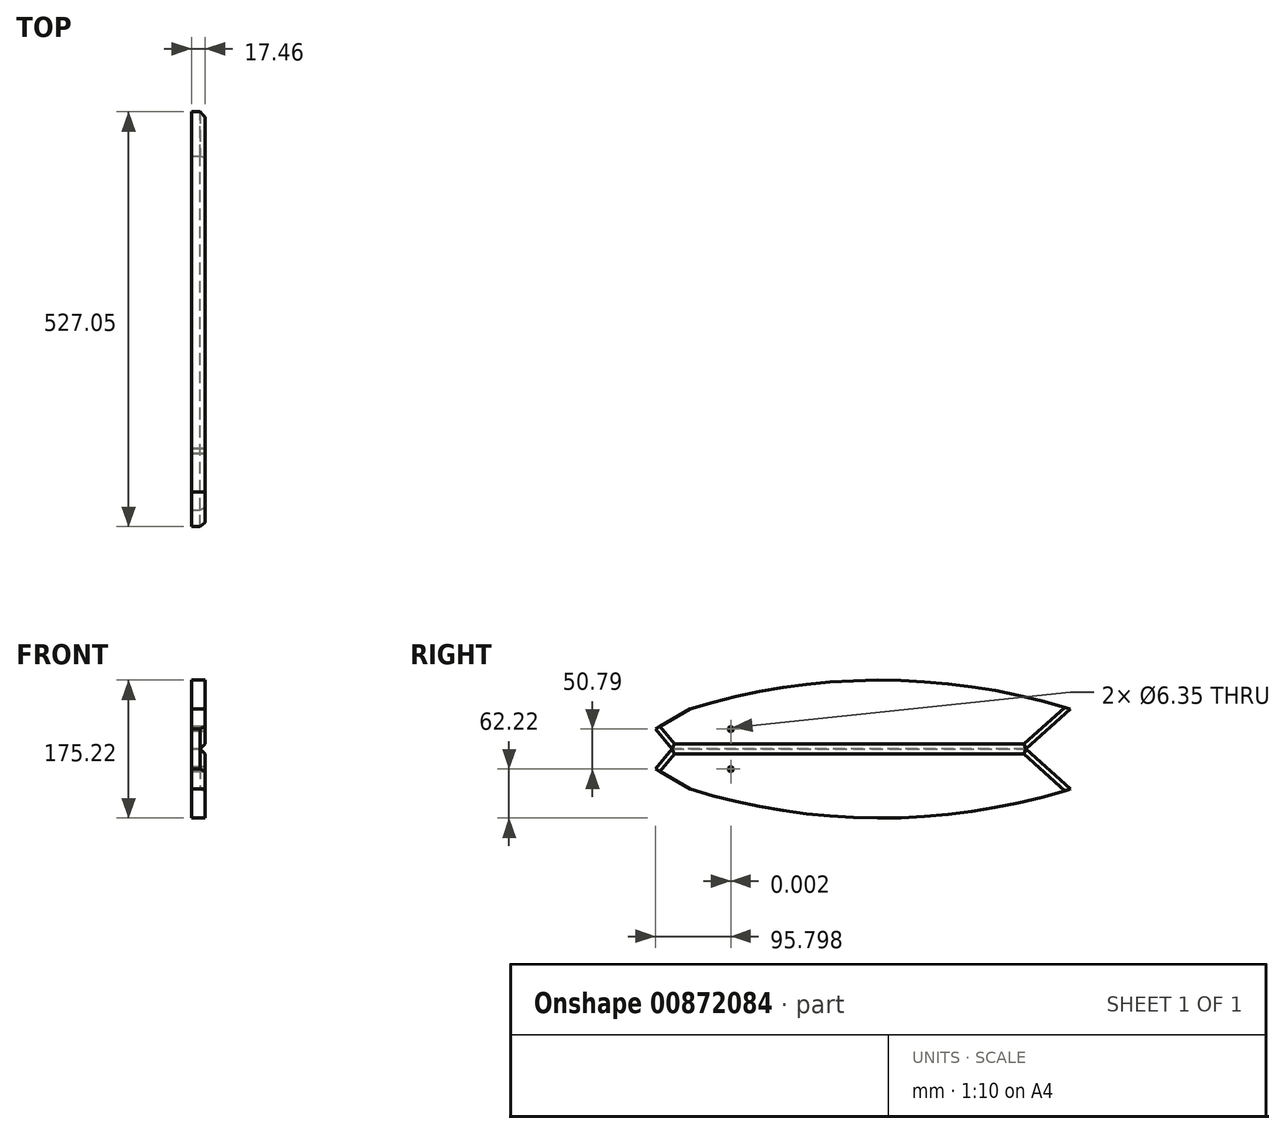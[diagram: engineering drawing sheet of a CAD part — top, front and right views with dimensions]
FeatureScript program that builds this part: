
annotation { "Feature Type Name" : "Feature", "Feature Type Description" : "" }
export const myFeature = defineFeature(function(context is Context, id is Id, definition is map)
    precondition{}
    {
        {
            var Q0;
            Q0=qCreatedBy(makeId("Right.planeOp"),FACE);
            var sketch = newSketch(context, id + "F0", { "sketchPlane" : qUnion([Q0])});
            skLineSegment(sketch, "E0.bottom", {"start": v(0, 0) * mm, "end": v(527.05, 0) * mm, "construction": true});
            skLineSegment(sketch, "E0.top", {"start": v(0, 87.31) * mm, "end": v(527.05, 87.31) * mm, "construction": true});
            skLineSegment(sketch, "E0.left", {"start": v(0, 0) * mm, "end": v(0, 87.31) * mm, "construction": true});
            skLineSegment(sketch, "E0.right", {"start": v(527.05, 0) * mm, "end": v(527.05, 87.31) * mm, "construction": true});
            skLineSegment(sketch, "E1", {"start": v(527.05, 50.8) * mm, "end": v(0, 50.8) * mm, "construction": true});
            skLineSegment(sketch, "E2", {"start": v(0, 25.4) * mm, "end": v(95.8, 25.4) * mm, "construction": true});
            skLineSegment(sketch, "E3", {"start": v(0, 25.4) * mm, "end": v(21.31, 0) * mm});
            skLineSegment(sketch, "E4", {"start": v(0, 25.4) * mm, "end": v(44, 50.8) * mm});
            skArc(sketch, "E5", {"start": v(527.05, 50.8) * mm, "mid": v(285.52, 87.61) * mm, "end": v(44, 50.8) * mm});
            skPoint(sketch, "E5.second.point", {"position": v(263.53, 87.31) * mm});
            skLineSegment(sketch, "E6", {"start": v(527.05, 50.8) * mm, "end": v(470.63, 0) * mm});
            skLineSegment(sketch, "E7", {"start": v(21.31, 0) * mm, "end": v(470.63, 0) * mm});
            skLineSegment(sketch, "E8", {"start": v(95.8, 25.4) * mm, "end": v(95.8, 0) * mm, "construction": true});
            skCircle(sketch, "E9", {"center": v(95.8, 25.4) * mm, "radius": 3.18 * mm});
            skSolve(sketch);
        }
        {
            var Q0;
            Q0=qSketchRegion(id+"F0",true);
            extrude(context, id + "F1", {"entities" : qUnion([Q0]), "depth" : 17.46 * mm});
        }
        {
            var Q0;
            Q0=qSketchRegion(id+"F0",true);
            extrude(context, id + "F2", {"entities" : qUnion([Q0]), "operationType" : NewBodyOperationType.ADD, "depth" : 17.46 * mm});
        }
        {
            var Q0;
            Q0=makeQuery(id+"F1.opExtrude","CAP_FACE",FACE,{"disambiguationData":[OSD([sQuery(id+"F0.wireOp",EDGE,"E3"),sQuery(id+"F0.wireOp",EDGE,"E4"),sQuery(id+"F0.wireOp",EDGE,"E5"),sQuery(id+"F0.wireOp",EDGE,"E6"),sQuery(id+"F0.wireOp",EDGE,"E7")])],"isStart":false});
            var sketch = newSketch(context, id + "F3", { "sketchPlane" : qUnion([Q0])});
            skLineSegment(sketch, "E10", {"start": v(21.31, 0) * mm, "end": v(222.49, -223.43) * mm, "construction": true});
            skLineSegment(sketch, "E11", {"start": v(222.49, -223.43) * mm, "end": v(470.63, 0) * mm, "construction": true});
            skCircle(sketch, "E12", {"center": v(95.8, 25.4) * mm, "radius": 3.17 * mm, "construction": true});
            skLineSegment(sketch, "E13", {"start": v(133.76, 48.8) * mm, "end": v(274.57, -176.54) * mm});
            skLineSegment(sketch, "E14", {"start": v(274.57, -176.54) * mm, "end": v(207.37, -237.04) * mm});
            skLineSegment(sketch, "E15", {"start": v(207.37, -237.04) * mm, "end": v(85.75, -42.4) * mm});
            skPoint(sketch, "E16.startSnap0", {"position": v(81.67, 46.5) * mm});
            skPoint(sketch, "E16.endSnap0", {"position": v(81.67, 46.5) * mm});
            skLineSegment(sketch, "E17", {"start": v(58.24, 1.62) * mm, "end": v(133.76, 48.8) * mm, "construction": true});
            skLineSegment(sketch, "E18", {"start": v(133.76, 48.8) * mm, "end": v(133.76, 48.8) * mm});
            skLineSegment(sketch, "E19", {"start": v(58.24, 1.62) * mm, "end": v(44.78, 23.16) * mm, "construction": true});
            skLineSegment(sketch, "E20", {"start": v(133.76, 48.8) * mm, "end": v(120.3, 70.35) * mm, "construction": true});
            skLineSegment(sketch, "E21", {"start": v(44.78, 23.16) * mm, "end": v(120.3, 70.35) * mm, "construction": true});
            skLineSegment(sketch, "E22", {"start": v(65.56, -10.1) * mm, "end": v(81.72, 0) * mm});
            skLineSegment(sketch, "E23", {"start": v(81.72, 0) * mm, "end": v(101.91, -32.31) * mm});
            skLineSegment(sketch, "E24", {"start": v(101.91, -32.31) * mm, "end": v(85.75, -42.4) * mm});
            skLineSegment(sketch, "E25.trimOffspring", {"start": v(65.56, -10.1) * mm, "end": v(58.24, 1.62) * mm});
            skSolve(sketch);
        }
        {
            var Q0;
            Q0=makeQuery(id+"F3.imprint","IMPRINT",FACE,{"disambiguationData":[TD([[makeQuery(id+"F3.imprint","IMPRINT",EDGE,{"derivedFrom":makeQuery(id+"F1.opExtrude","CAP_EDGE",EDGE,{"disambiguationData":[OSD([sQuery(id+"F0.wireOp",EDGE,"E3")])],"isStart":false})}),1.0]])]});
            var sketch = newSketch(context, id + "F4", { "sketchPlane" : qUnion([Q0])});
            skLineSegment(sketch, "E26.MirrorCS", {"start": v(0, -25.38) * mm, "end": v(21.31, 0.01) * mm});
            skLineSegment(sketch, "E27.MirrorCS", {"start": v(0, -25.38) * mm, "end": v(44, -50.79) * mm});
            skArc(sketch, "E28.MirrorCS", {"start": v(527.05, -50.82) * mm, "mid": v(285.52, -87.61) * mm, "end": v(44, -50.79) * mm});
            skLineSegment(sketch, "E29.MirrorCS", {"start": v(527.05, -50.82) * mm, "end": v(470.63, -0.01) * mm});
            skCircle(sketch, "E30.MirrorC", {"center": v(95.8, -25.4) * mm, "radius": 3.18 * mm});
            skLineSegment(sketch, "E31", {"start": v(21.31, 0.01) * mm, "end": v(470.63, -0.01) * mm});
            skSolve(sketch);
        }
        {
            var Q0;
            Q0=qSketchRegion(id+"F4",true);
            extrude(context, id + "F5", {"entities" : qUnion([Q0]), "depth" : -17.46 * mm});
        }
        {
            var Q0;
            Q0=makeQuery(id+"F1.opExtrude","CAP_EDGE",EDGE,{"disambiguationData":[OSD([sQuery(id+"F0.wireOp",EDGE,"E3")])],"isStart":false});
            var Q1;
            Q1=makeQuery(id+"F1.opExtrude","CAP_EDGE",EDGE,{"disambiguationData":[OSD([sQuery(id+"F0.wireOp",EDGE,"E7")])],"isStart":false});
            var Q2;
            Q2=makeQuery(id+"F1.opExtrude","CAP_EDGE",EDGE,{"disambiguationData":[OSD([sQuery(id+"F0.wireOp",EDGE,"E6")])],"isStart":false});
            var Q3;
            Q3=makeQuery(id+"F5.opExtrude","CAP_EDGE",EDGE,{"disambiguationData":[OSD([sQuery(id+"F4.wireOp",EDGE,"E29.MirrorCS")])],"isStart":true});
            var Q4;
            Q4=makeQuery(id+"F5.opExtrude","CAP_EDGE",EDGE,{"disambiguationData":[OSD([sQuery(id+"F4.wireOp",EDGE,"E31")])],"isStart":true});
            var Q5;
            Q5=makeQuery(id+"F5.opExtrude","CAP_EDGE",EDGE,{"disambiguationData":[OSD([sQuery(id+"F4.wireOp",EDGE,"E26.MirrorCS")])],"isStart":true});
            chamfer(context, id + "F6", {"entities" : qUnion([Q0, Q1, Q2, Q3, Q4, Q5]), "width" : 6.35 * mm, "tangentPropagation" : true});
        }
    });
